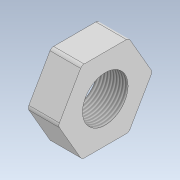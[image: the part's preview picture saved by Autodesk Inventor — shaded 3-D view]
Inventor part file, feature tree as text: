
AUTODESK INVENTOR PART (.ipt)
format: ipt  version: 2021 (Build 250183000, 183)  size: 111,104 bytes
history: native  units: mm
features: other x1, extrude x1, hole x1, fillet x1, sketch x1
ambient origin geometry x8: Origin, YZ Plane, XZ Plane, XY Plane, X Axis, Y Axis, Z Axis, Center Point
bodies: Body1 (feature_tree)
feature tree (5):
  other  "Sólido1"
  extrude  "Extrusión1"  Depth=2.0mm
  hole  "Agujero1"  [1 undecoded]
  fillet  "Empalme1"  Radius=15.0mm
  sketch  "Boceto1"  dims[d1=60.0deg d2=20.0mm d3=60.0mm d5=360.0deg d7=15.0mm d8=0.0mm d9=10.0mm d10=10.0mm d11=22.376202mm d12=48.0mm d13=4.0mm d14=2.0mm d15=90.0deg d16=8.0mm d17=20.594885mm d18=2.0mm]
note: 1 required parameter value undecoded (feature->parameter linkage not recoverable at this tier; creation-order binding heuristic only, values carry confidence <= 0.55)
